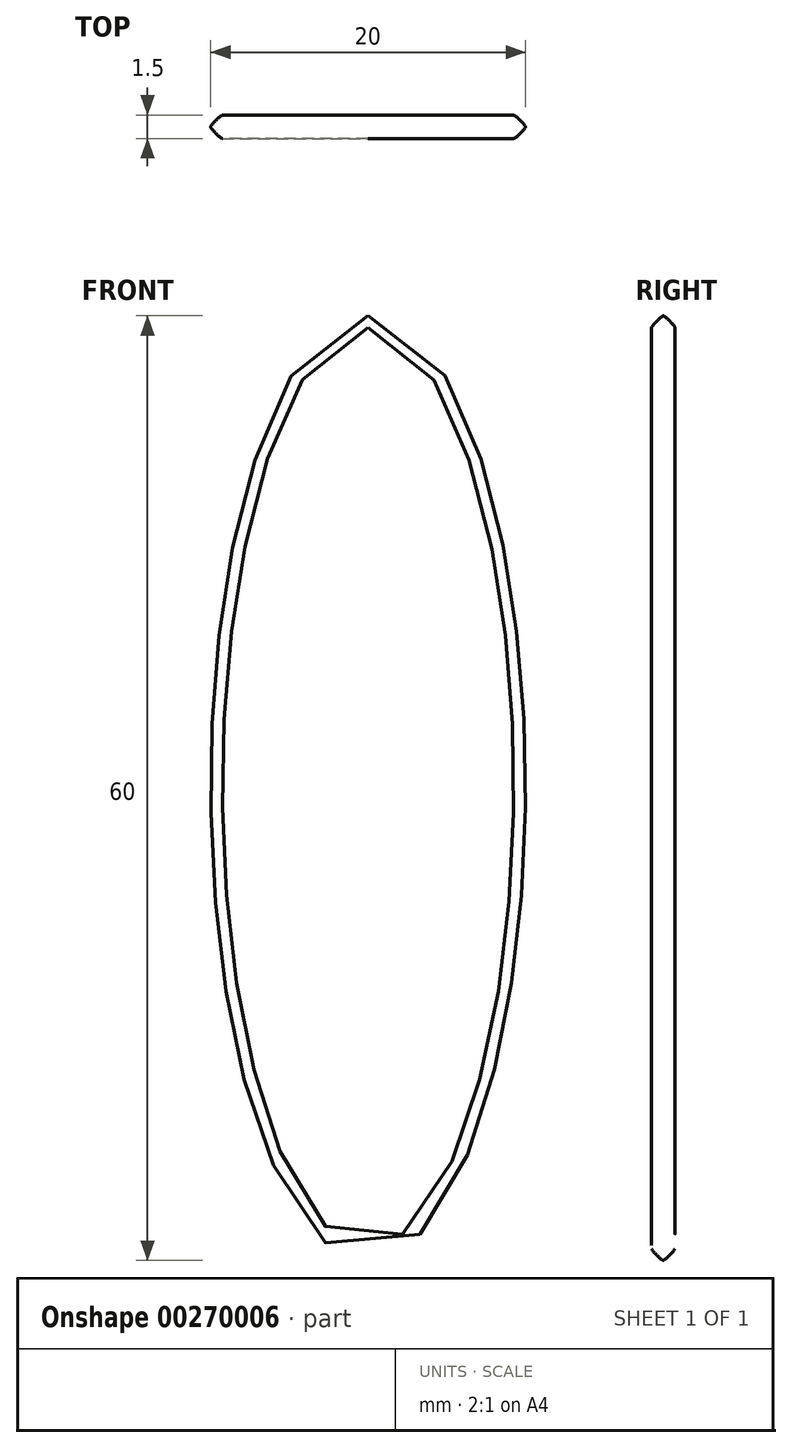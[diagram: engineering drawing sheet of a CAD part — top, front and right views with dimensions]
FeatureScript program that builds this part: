
annotation { "Feature Type Name" : "Feature", "Feature Type Description" : "" }
export const myFeature = defineFeature(function(context is Context, id is Id, definition is map)
    precondition{}
    {
        {
            var Q0;
            Q0=qCreatedBy(makeId("Front.planeOp"),FACE);
            var sketch = newSketch(context, id + "F0", { "sketchPlane" : qUnion([Q0])});
            skEllipse(sketch, "E0", {"center": v(0, 0) * mm, "majorRadius": 30 * mm, "minorRadius": 10 * mm, "majorAxis": v(0, 1)});
            skLineSegment(sketch, "E1", {"start": v(0, 0) * mm, "end": v(-10, 0) * mm});
            skSolve(sketch);
        }
        {
            var Q0;
            Q0=makeQuery(id+"F0.imprint","IMPRINT",FACE,{"disambiguationData":[TD([[makeQuery(id+"F0.imprint","IMPRINT",EDGE,{"derivedFrom":sQuery(id+"F0.wireOp",EDGE,"E0")}),1.0]])]});
            extrude(context, id + "F1", {"entities" : qUnion([Q0]), "depth" : 1.5 * mm});
        }
        {
            var Q0;
            Q0=makeQuery(id+"F1.opExtrude","CAP_EDGE",EDGE,{"disambiguationData":[OSD([sQuery(id+"F0.wireOp",EDGE,"E0")])],"isStart":false});
            var Q1;
            Q1=makeQuery(id+"F1.opExtrude","CAP_EDGE",EDGE,{"disambiguationData":[OSD([sQuery(id+"F0.wireOp",EDGE,"E0")])],"isStart":true});
            fillet(context, id + "F2", {"entities" : qUnion([Q0, Q1]), "radius" : 0.75 * mm, "tangentPropagation" : true, "rho" : 0.1, "crossSection" : FilletCrossSection.CONIC, "allowEdgeOverflow" : false});
        }
    });
